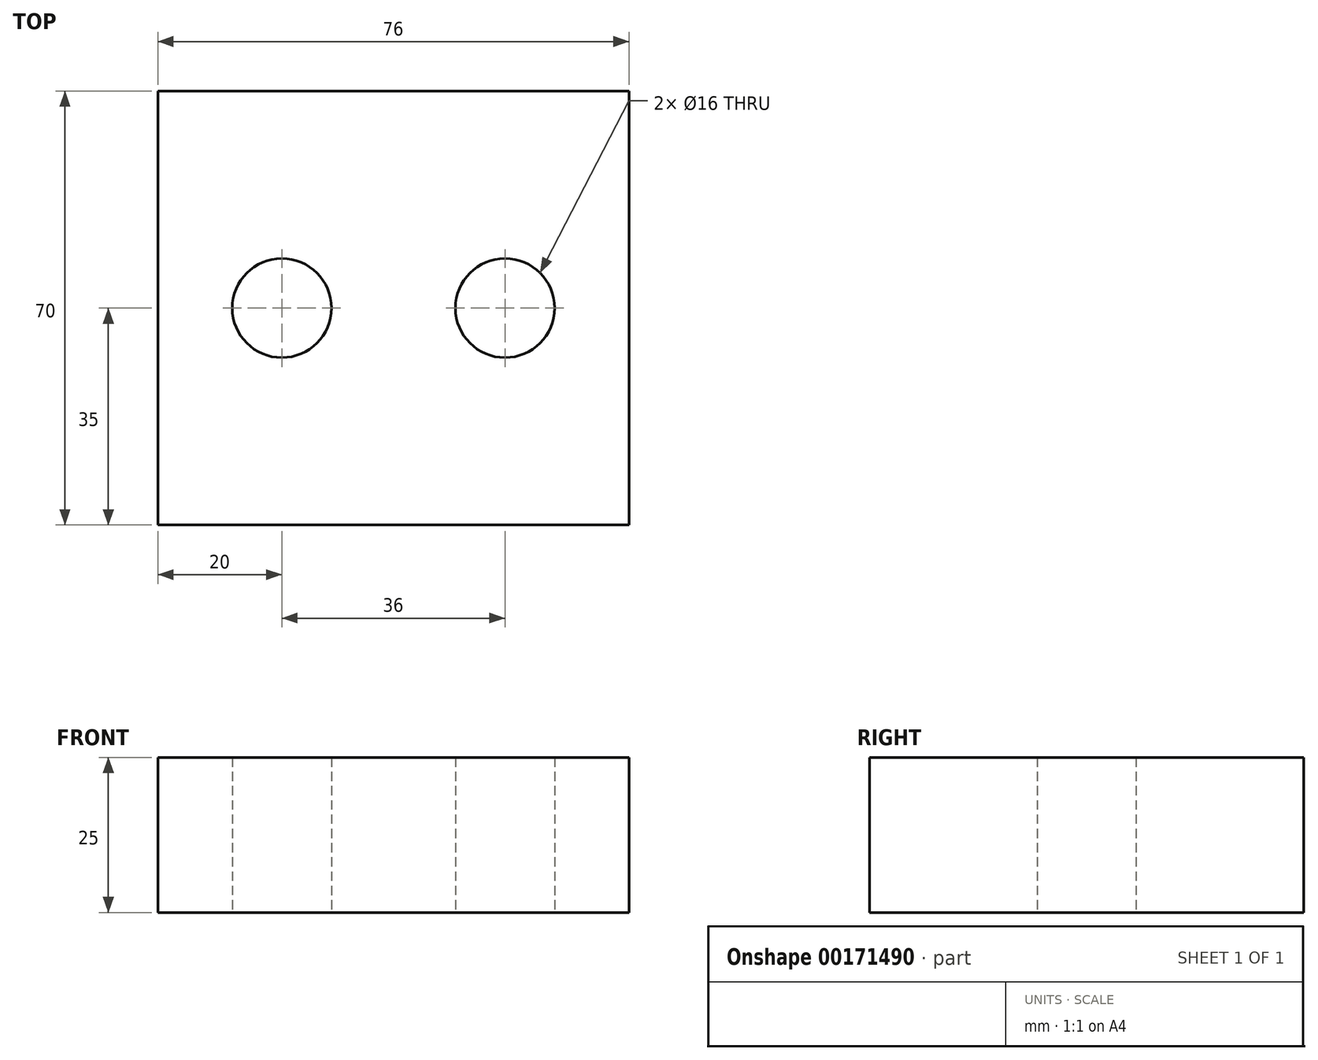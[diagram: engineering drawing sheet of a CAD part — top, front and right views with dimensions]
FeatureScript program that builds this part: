
annotation { "Feature Type Name" : "Feature", "Feature Type Description" : "" }
export const myFeature = defineFeature(function(context is Context, id is Id, definition is map)
    precondition{}
    {
        {
            var Q0;
            Q0=qCreatedBy(makeId("Top.planeOp"),FACE);
            var sketch = newSketch(context, id + "F0", { "sketchPlane" : qUnion([Q0])});
            skLineSegment(sketch, "E0.bottom", {"start": v(0, 0) * mm, "end": v(76, 0) * mm});
            skLineSegment(sketch, "E0.top", {"start": v(0, 70) * mm, "end": v(76, 70) * mm});
            skLineSegment(sketch, "E0.left", {"start": v(0, 0) * mm, "end": v(0, 70) * mm});
            skLineSegment(sketch, "E0.right", {"start": v(76, 0) * mm, "end": v(76, 70) * mm});
            skCircle(sketch, "E1", {"center": v(20, 35) * mm, "radius": 8 * mm});
            skLineSegment(sketch, "E2", {"start": v(20, 35) * mm, "end": v(0, 35) * mm, "construction": true});
            skCircle(sketch, "E3", {"center": v(56, 35) * mm, "radius": 8 * mm});
            skSolve(sketch);
        }
        {
            var Q0;
            Q0=makeQuery(id+"F0.imprint","IMPRINT",FACE,{"disambiguationData":[TD([[makeQuery(id+"F0.imprint","IMPRINT",EDGE,{"derivedFrom":sQuery(id+"F0.wireOp",EDGE,"E0.bottom")}),1.0]])]});
            extrude(context, id + "F1", {"entities" : qUnion([Q0]), "depth" : 25 * mm});
        }
    });
